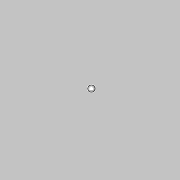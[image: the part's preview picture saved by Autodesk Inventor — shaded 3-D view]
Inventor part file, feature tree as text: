
AUTODESK INVENTOR PART (.ipt)
format: ipt  version: 2017 (Build 210142000, 142)  size: 135,680 bytes
history: native  units: mm
features: sketch x9, extrude x8, revolve x2
ambient origin geometry x8: Origin, YZ Plane, XZ Plane, XY Plane, X Axis, Y Axis, Z Axis, Center Point
feature tree (19):
  extrude  "Extrusion2"  Depth=120.0mm TaperAngle=0.0deg
  extrude  "Extrusion3"  Depth=15.0mm TaperAngle=0.0deg
  extrude  "Extrusion4"  Depth=8.0mm TaperAngle=0.0deg
  extrude  "Extrusion5"  Depth=50.0mm TaperAngle=0.0deg
  extrude  "Extrusion6"  Depth=25.0mm TaperAngle=0.0deg
  extrude  "Extrusion7"  Depth=50.0mm TaperAngle=0.0deg
  sketch  "Sketch10"  dims[d20=15.0mm d21=12.5mm]
  revolve  "Revolution1"  [1 undecoded]
  extrude  "Extrusion8"  Depth=50.0mm TaperAngle=0.0deg
  extrude  "Extrusion9"  TaperAngle=90.0deg  [1 undecoded]
  revolve  "Revolution2"  [1 undecoded]
  sketch  "Sketch4"  dims[d2=9.0mm d3=120.0mm d4=0.0mm]
  sketch  "Sketch5"  dims[d5=19.05mm d6=15.0mm d7=0.0mm]
  sketch  "Sketch6"  dims[d8=24.0mm d9=8.0mm d10=0.0mm]
  sketch  "Sketch7"  dims[d11=9.0mm d12=50.0mm d13=0.0mm]
  sketch  "Sketch8"  dims[d14=25.0mm d15=25.0mm d16=0.0mm]
  sketch  "Sketch9"  dims[d17=50.0mm d18=50.0mm d19=0.0mm]
  sketch  "Sketch11"  dims[d22=90.0deg d23=50.0mm d24=0.0mm]
  sketch  "Sketch12"  dims[d25=5.0mm d26=0.0mm d27=90.0deg d28=0.0mm]
note: 3 required parameter values undecoded (feature->parameter linkage not recoverable at this tier; creation-order binding heuristic only, values carry confidence <= 0.55)